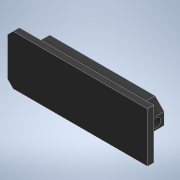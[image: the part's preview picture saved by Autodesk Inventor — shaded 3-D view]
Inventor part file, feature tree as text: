
AUTODESK INVENTOR PART (.ipt)
format: ipt  version: 2021 (Build 250183000, 183)  size: 144,896 bytes
history: native  units: mm
features: extrude x3, sketch x3, mirror x1, projected_geometry x1
ambient origin geometry x8: Origin, YZ Plane, XZ Plane, XY Plane, X Axis, Y Axis, Z Axis, Center Point
bodies: Solid1 (feature_tree)
feature tree (8):
  extrude  "Extrusion1"  Depth=3.0mm
  extrude  "Extrusion4"  Depth=10.0mm
  extrude  "Extrusion5"  Depth=6.0mm TaperAngle=0.0deg
  mirror  "Mirror1"
  sketch  "Sketch1"  dims[d0=3.0mm d1=3.0mm]
  sketch  "Sketch4"  dims[d2=10.0mm d3=34.0mm]
  projected_geometry  "Projected Loop2"
  sketch  "Sketch5"  dims[d4=0.15mm d5=6.0mm d6=0.0mm d20=45.0mm d21=16.0mm d22=1.8mm d23=1.8mm d24=1.8mm d25=22.5mm d26=2.0mm d27=0.0mm d28=3.5mm d29=2.8mm d30=8.0mm d31=0.0mm]
